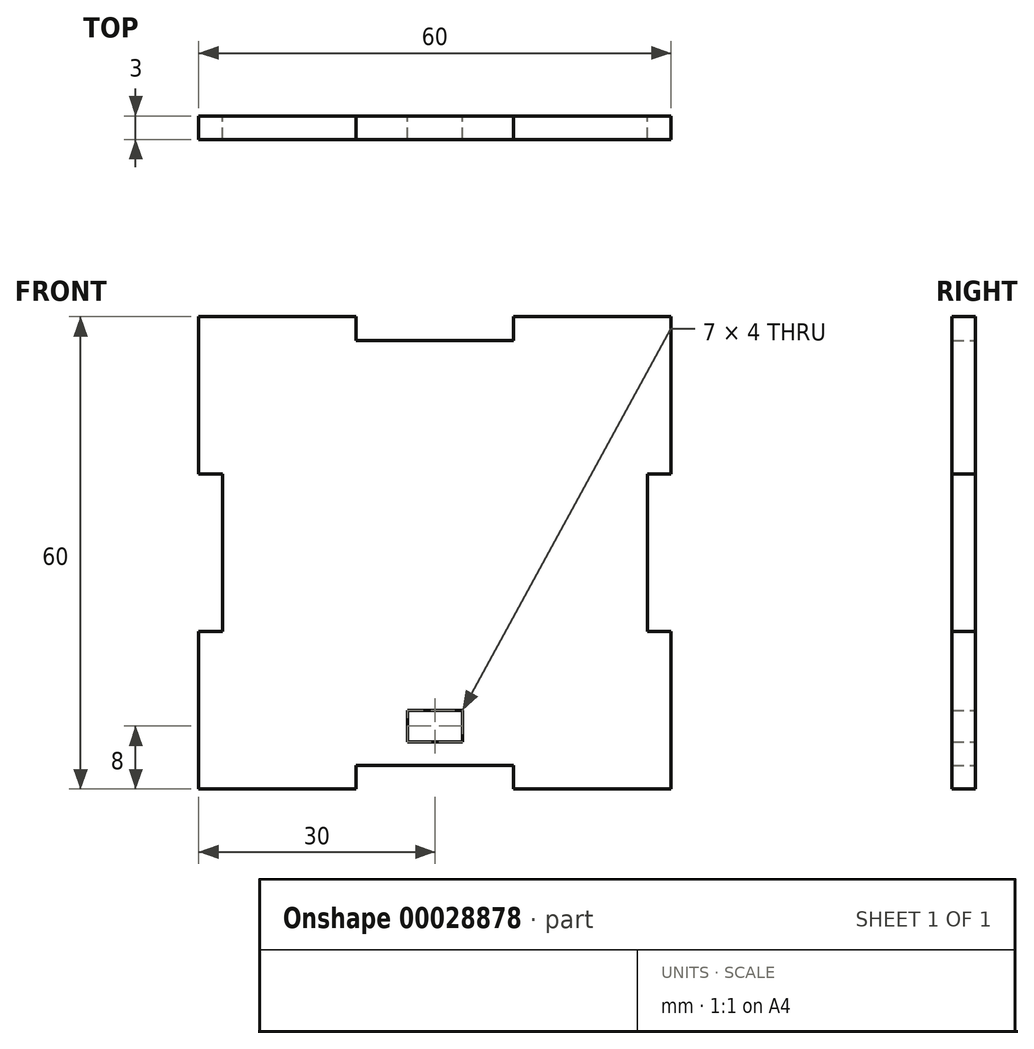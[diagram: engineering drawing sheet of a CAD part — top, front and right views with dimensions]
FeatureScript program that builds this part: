
annotation { "Feature Type Name" : "Feature", "Feature Type Description" : "" }
export const myFeature = defineFeature(function(context is Context, id is Id, definition is map)
    precondition{}
    {
        {
            var Q0;
            Q0=qCreatedBy(makeId("Front.planeOp"),FACE);
            var sketch = newSketch(context, id + "F0", { "sketchPlane" : qUnion([Q0])});
            skLineSegment(sketch, "E0", {"start": v(0, 27) * mm, "end": v(-10, 27) * mm});
            skLineSegment(sketch, "E1", {"start": v(-10, 27) * mm, "end": v(-10, 30) * mm});
            skLineSegment(sketch, "E2", {"start": v(-10, 30) * mm, "end": v(-30, 30) * mm});
            skLineSegment(sketch, "E3", {"start": v(-30, 30) * mm, "end": v(-30, 10) * mm});
            skLineSegment(sketch, "E4", {"start": v(-30, 10) * mm, "end": v(-27, 10) * mm});
            skLineSegment(sketch, "E5", {"start": v(-27, 10) * mm, "end": v(-27, 0) * mm});
            skLineSegment(sketch, "E6.MirrorCS", {"start": v(30, 10) * mm, "end": v(27, 10) * mm});
            skLineSegment(sketch, "E7.MirrorCS", {"start": v(10, 27) * mm, "end": v(10, 30) * mm});
            skLineSegment(sketch, "E8.MirrorCS", {"start": v(27, 10) * mm, "end": v(27, 0) * mm});
            skLineSegment(sketch, "E9.MirrorCS", {"start": v(0, 27) * mm, "end": v(10, 27) * mm});
            skLineSegment(sketch, "E10.MirrorCS", {"start": v(30, 30) * mm, "end": v(30, 10) * mm});
            skLineSegment(sketch, "E11.MirrorCS", {"start": v(10, 30) * mm, "end": v(30, 30) * mm});
            skLineSegment(sketch, "E12.MirrorCS", {"start": v(-10, -27) * mm, "end": v(-10, -30) * mm});
            skLineSegment(sketch, "E13.MirrorCS", {"start": v(30, -10) * mm, "end": v(27, -10) * mm});
            skLineSegment(sketch, "E14.MirrorCS", {"start": v(10, -27) * mm, "end": v(10, -30) * mm});
            skLineSegment(sketch, "E15.MirrorCS", {"start": v(-30, -10) * mm, "end": v(-27, -10) * mm});
            skLineSegment(sketch, "E16.MirrorCS", {"start": v(30, -30) * mm, "end": v(30, -10) * mm});
            skLineSegment(sketch, "E17.MirrorCS", {"start": v(-27, -10) * mm, "end": v(-27, 0) * mm});
            skLineSegment(sketch, "E18.MirrorCS", {"start": v(0, -27) * mm, "end": v(-10, -27) * mm});
            skLineSegment(sketch, "E19.MirrorCS", {"start": v(10, -30) * mm, "end": v(30, -30) * mm});
            skLineSegment(sketch, "E20.MirrorCS", {"start": v(-10, -30) * mm, "end": v(-30, -30) * mm});
            skLineSegment(sketch, "E21.MirrorCS", {"start": v(-30, -30) * mm, "end": v(-30, -10) * mm});
            skLineSegment(sketch, "E22.MirrorCS", {"start": v(0, -27) * mm, "end": v(10, -27) * mm});
            skLineSegment(sketch, "E23.MirrorCS", {"start": v(27, -10) * mm, "end": v(27, 0) * mm});
            skSolve(sketch);
        }
        {
            var Q0;
            Q0=makeQuery(id+"F0.imprint","IMPRINT",FACE,{"disambiguationData":[TD([[makeQuery(id+"F0.imprint","IMPRINT",EDGE,{"derivedFrom":sQuery(id+"F0.wireOp",EDGE,"E4")}),1.0]])]});
            extrude(context, id + "F1", {"entities" : qUnion([Q0]), "depth" : 3 * mm});
        }
        {
            var Q0;
            Q0=qCreatedBy(makeId("Front.planeOp"),FACE);
            var sketch = newSketch(context, id + "F2", { "sketchPlane" : qUnion([Q0])});
            skLineSegment(sketch, "E24.rect.bottom", {"start": v(3.5, -24) * mm, "end": v(-3.5, -24) * mm});
            skLineSegment(sketch, "E24.rect.top", {"start": v(3.5, -20) * mm, "end": v(-3.5, -20) * mm});
            skLineSegment(sketch, "E24.rect.left", {"start": v(3.5, -24) * mm, "end": v(3.5, -20) * mm});
            skLineSegment(sketch, "E24.rect.right", {"start": v(-3.5, -24) * mm, "end": v(-3.5, -20) * mm});
            skPoint(sketch, "E24.rect.middle", {"position": v(0, -22) * mm});
            skSolve(sketch);
        }
        {
            var Q0;
            Q0=makeQuery(id+"F2.imprint","IMPRINT",FACE,{"disambiguationData":[TD([[makeQuery(id+"F2.imprint","IMPRINT",EDGE,{"derivedFrom":sQuery(id+"F2.wireOp",EDGE,"E24.rect.bottom")}),-1.0]])]});
            extrude(context, id + "F3", {"entities" : qUnion([Q0]), "operationType" : NewBodyOperationType.REMOVE, "depth" : 25 * mm});
        }
    });
